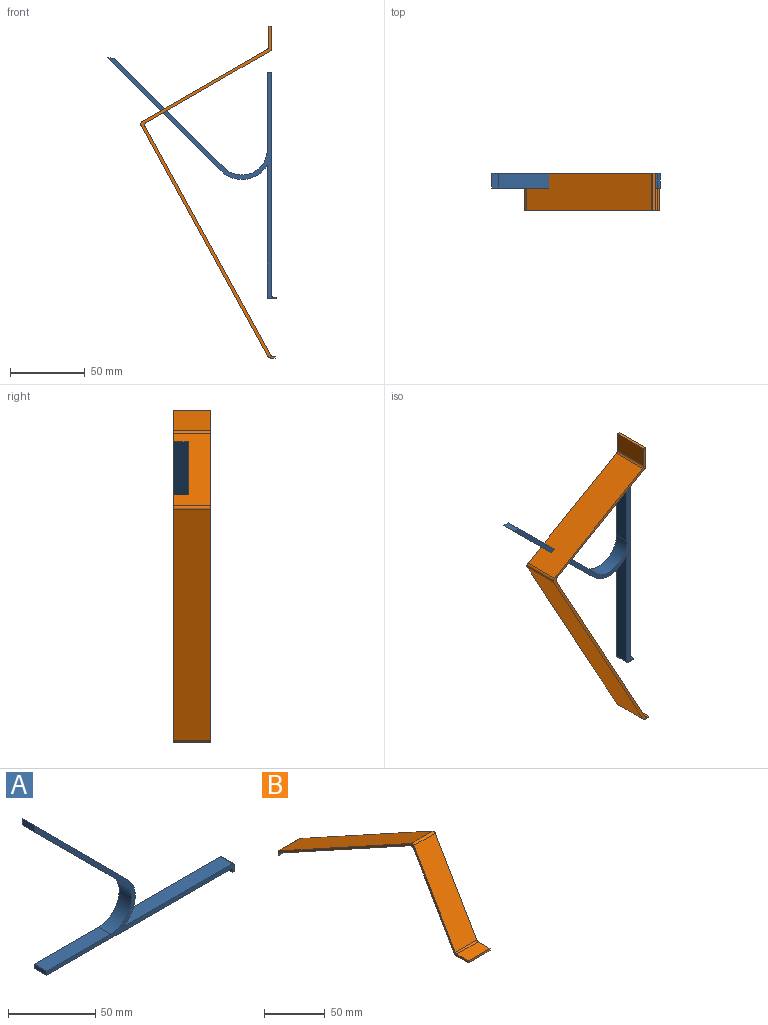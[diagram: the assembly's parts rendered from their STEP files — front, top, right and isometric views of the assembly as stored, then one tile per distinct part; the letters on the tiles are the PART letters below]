
ASSEMBLY  parts=2 mates=2
PART A: 16 faces, bbox 161.7x10x113 mm
  f0: cylinder r=20mm len=31.14mm, axis (0,1,0), area 360.3mm2, adj f3,f5,f6,f10
  f1: plane 10x4.67mm, normal (-1,0,-0.09), area 46.9mm2, adj f3,f5,f6,f9
  f2: plane 149.72x10mm, normal (0,0,-1), area 1497.2mm2, adj f4,f5,f6,f14
  f3: plane 75.86x75.86mm, normal (0.71,0,0.71), area 1072.8mm2, adj f0,f1,f5,f6
  f4: plane 10x3mm, normal (-1,0,-0.09), area 30.1mm2, adj f2,f5,f6,f7
  f5: plane 161.72x113mm, normal (0,-1,0), area 884.4mm2, adj f0,f1,f2,f3,f4,f7,f8,f9
  f6: plane 161.72x113mm, normal (0,1,0), area 884.4mm2, adj f0,f1,f2,f3,f4,f7,f8,f9
  f7: plane 51.99x10mm, normal (0,0,1), area 519.9mm2, adj f4,f5,f6,f8
  f8: cylinder r=17mm len=29.02mm, axis (0,1,0), area 400.6mm2, adj f5,f6,f7,f9
  f9: plane 73.31x73.31mm, normal (-0.71,0,-0.71), area 1036.8mm2, adj f1,f5,f6,f8
  f10: plane 88.46x10mm, normal (0,0,1), area 884.6mm2, adj f0,f5,f6,f15
  f11: plane 10x2mm, normal (-1,0,0), area 20mm2, adj f5,f6,f12,f14
  f12: plane 10x1mm, normal (0,0,-1), area 10mm2, adj f5,f6,f11,f13
  f13: plane 10x5mm, normal (1,0,0), area 50mm2, adj f5,f6,f12,f15
  f14: cylinder r=1mm len=10mm, axis (0,1,0), area 15.7mm2, adj f2,f5,f6,f11
  f15: cylinder r=1mm len=10mm, axis (0,-1,0), area 15.7mm2, adj f5,f6,f10,f13
PART B: 18 faces, bbox 25x222.8x90.2 mm
  f0: plane 153.29x84.13mm, normal (0,-0.48,-0.88), area 4371.5mm2, adj f1,f2,f12,f13
  f1: plane 222.8x90.19mm, normal (1,0,0), area 591.8mm2, adj f0,f3,f4,f5,f6,f7,f8,f9
  f2: plane 222.8x90.19mm, normal (-1,0,0), area 591.8mm2, adj f0,f3,f4,f5,f6,f7,f8,f9
  f3: plane 25x3.1mm, normal (0,1,0), area 77.4mm2, adj f1,f2,f11,f15
  f4: plane 25x2mm, normal (0,-1,0), area 50mm2, adj f1,f2,f5,f8
  f5: plane 25x13.85mm, normal (0,0,1), area 346.1mm2, adj f1,f2,f4,f17
  f6: plane 155.04x85.09mm, normal (0,0.48,0.88), area 4421.5mm2, adj f1,f2,f15,f16
  f7: plane 83.91x48.44mm, normal (0,-0.87,0.5), area 2422.2mm2, adj f1,f2,f16,f17
  f8: plane 25x15mm, normal (0,0,-1), area 375mm2, adj f1,f2,f4,f14
  f9: plane 83.21x48.04mm, normal (0,0.87,-0.5), area 2402.1mm2, adj f1,f2,f13,f14
  f10: plane 25x1.37mm, normal (0,-1,0), area 34.1mm2, adj f1,f2,f11,f12
  f11: plane 25x1mm, normal (0,0,-1), area 25mm2, adj f1,f2,f3,f10
  f12: cylinder r=2mm len=25mm, axis (1,0,0), area 53.4mm2, adj f0,f1,f2,f10
  f13: cylinder r=2mm len=25mm, axis (1,0,0), area 77.5mm2, adj f0,f1,f2,f9
  f14: cylinder r=2mm len=25mm, axis (-1,0,0), area 52.4mm2, adj f1,f2,f8,f9
  f15: cylinder r=2mm len=25mm, axis (-1,0,0), area 53.4mm2, adj f1,f2,f3,f6
  f16: cylinder r=2mm len=25mm, axis (-1,0,0), area 77.5mm2, adj f1,f2,f6,f7
  f17: cylinder r=2mm len=25mm, axis (1,0,0), area 52.4mm2, adj f1,f2,f5,f7
PLACE A rot(axis=(0.71,0,-0.71),180deg) t=(34.96,-83.81,-2.79)mm
PLACE B rot(axis=(-0.58,-0.58,0.58),120deg) t=(32.96,-103.81,-10.64)mm
MATE planar B.f1 <-> A.f5  axis (0,1,0) through (-6.67,-78.81,-47.98)mm
MATE planar B.f8 <-> A.f2  axis (1,0,0) through (34.96,-91.31,46.86)mm
